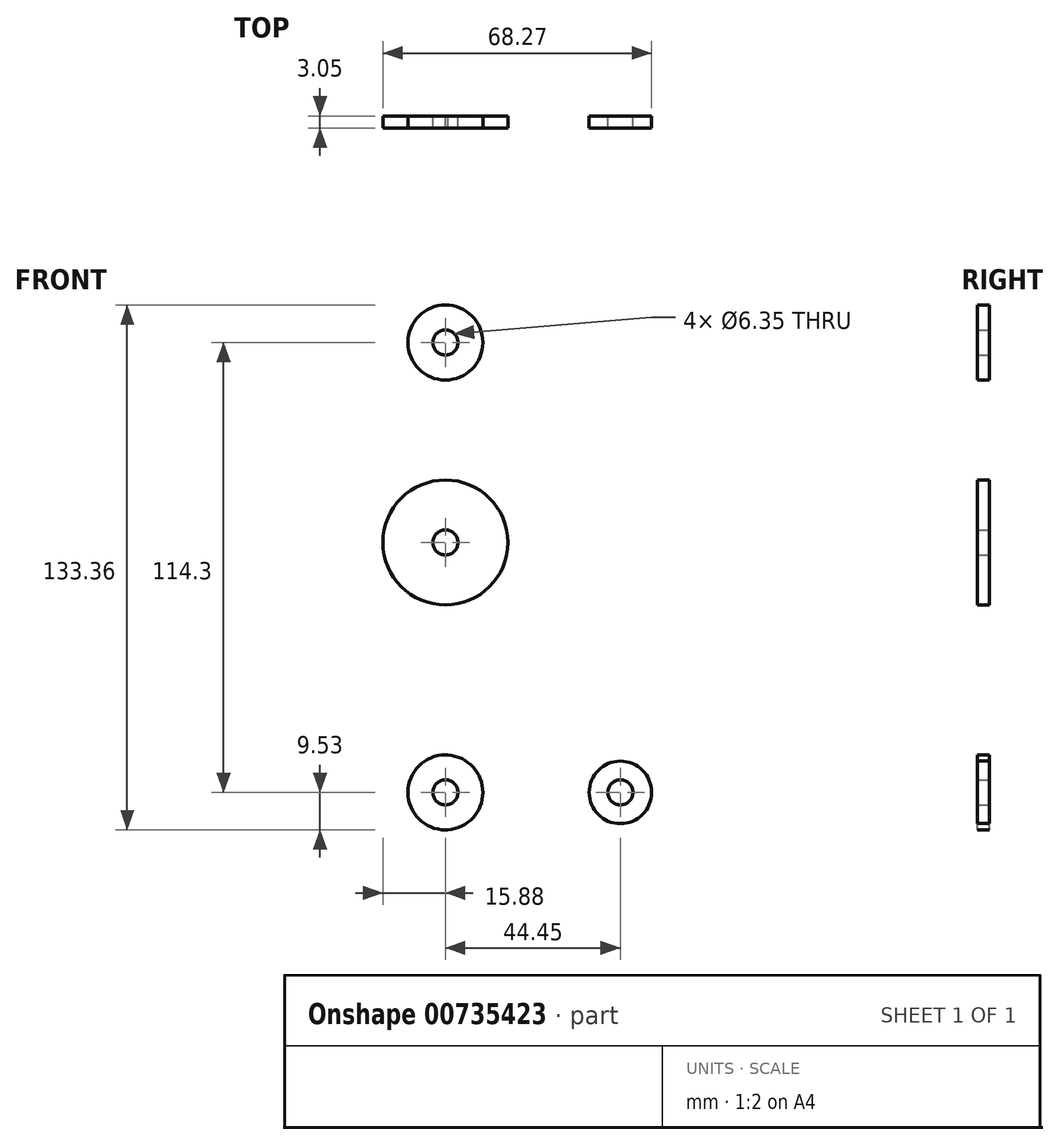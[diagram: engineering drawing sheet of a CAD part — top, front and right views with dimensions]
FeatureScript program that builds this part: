
annotation { "Feature Type Name" : "Feature", "Feature Type Description" : "" }
export const myFeature = defineFeature(function(context is Context, id is Id, definition is map)
    precondition{}
    {
        {
            var Q0;
            Q0=qCreatedBy(makeId("Front.planeOp"),FACE);
            var sketch = newSketch(context, id + "F0", { "sketchPlane" : qUnion([Q0])});
            skLineSegment(sketch, "E0", {"start": v(0, 0) * mm, "end": v(44.45, 0) * mm, "construction": true});
            skLineSegment(sketch, "E1", {"start": v(0, 0) * mm, "end": v(0, 114.3) * mm, "construction": true});
            skCircle(sketch, "E2", {"center": v(0, 114.3) * mm, "radius": 9.53 * mm});
            skCircle(sketch, "E3", {"center": v(0, 0) * mm, "radius": 9.53 * mm});
            skCircle(sketch, "E4", {"center": v(44.45, 0) * mm, "radius": 7.94 * mm});
            skCircle(sketch, "E5", {"center": v(0, 63.5) * mm, "radius": 15.88 * mm});
            skLineSegment(sketch, "E6", {"start": v(0, 9.53) * mm, "end": v(0.68, 9.5) * mm});
            skLineSegment(sketch, "E7", {"start": v(44.73, 7.93) * mm, "end": v(18.96, 8.85) * mm});
            skLineSegment(sketch, "E8", {"start": v(0, -9.53) * mm, "end": v(44.73, -7.93) * mm});
            skLineSegment(sketch, "E9", {"start": v(44.73, -7.93) * mm, "end": v(0, -9.53) * mm});
            skLineSegment(sketch, "E10", {"start": v(-9.45, 115.5) * mm, "end": v(-15.75, 65.48) * mm});
            skLineSegment(sketch, "E11", {"start": v(-15.75, 65.48) * mm, "end": v(-9.45, 115.5) * mm});
            skLineSegment(sketch, "E12", {"start": v(9.45, 115.5) * mm, "end": v(15.75, 65.48) * mm});
            skLineSegment(sketch, "E13", {"start": v(15.75, 65.48) * mm, "end": v(9.45, 115.5) * mm});
            skLineSegment(sketch, "E14", {"start": v(15.75, 61.91) * mm, "end": v(11.33, 17.58) * mm});
            skLineSegment(sketch, "E15", {"start": v(11.33, 17.58) * mm, "end": v(15.75, 61.91) * mm});
            skLineSegment(sketch, "E16", {"start": v(-15.8, 61.91) * mm, "end": v(-9.48, -0.95) * mm});
            skLineSegment(sketch, "E17", {"start": v(-9.48, -0.95) * mm, "end": v(-15.8, 61.91) * mm});
            skCircle(sketch, "E18", {"center": v(0, 114.3) * mm, "radius": 3.18 * mm});
            skCircle(sketch, "E19", {"center": v(-3.11, 99.9) * mm, "radius": 3.18 * mm});
            skCircle(sketch, "E20", {"center": v(0, 63.5) * mm, "radius": 3.18 * mm});
            skCircle(sketch, "E21", {"center": v(0, 0) * mm, "radius": 3.18 * mm});
            skCircle(sketch, "E22", {"center": v(44.45, 0) * mm, "radius": 3.18 * mm});
            skArc(sketch, "E23.filletArc", {"start": v(11.33, 17.58) * mm, "mid": v(13.25, 11.57) * mm, "end": v(18.96, 8.85) * mm});
            skLineSegment(sketch, "E24.trimOffspring", {"start": v(18.96, 8.85) * mm, "end": v(44.73, 7.93) * mm});
            skLineSegment(sketch, "E25.trimOffspring", {"start": v(9.57, 0) * mm, "end": v(9.48, -0.95) * mm});
            skSolve(sketch);
        }
        {
            var Q0;
            {var subQ1=sQuery(id+"F0.wireOp",EDGE,"E11");Q0=makeQuery(id+"F0.imprint","IMPRINT",FACE,{"disambiguationData":[TD([[makeQuery(id+"F0.imprint","IMPRINT",EDGE,{"derivedFrom":subQ1}),-1.0]])]});}
            var Q1;
            Q1=makeQuery(id+"F0.imprint","IMPRINT",FACE,{"disambiguationData":[TD([[makeQuery(id+"F0.imprint","IMPRINT",EDGE,{"derivedFrom":sQuery(id+"F0.wireOp",EDGE,"E18")}),-1.0]])]});
            var Q2;
            Q2=makeQuery(id+"F0.imprint","IMPRINT",FACE,{"disambiguationData":[TD([[makeQuery(id+"F0.imprint","IMPRINT",EDGE,{"derivedFrom":sQuery(id+"F0.wireOp",EDGE,"E20")}),-1.0]])]});
            var Q3;
            {var subQ0=sQuery(id+"F0.wireOp",EDGE,"E17");Q3=makeQuery(id+"F0.imprint","IMPRINT",FACE,{"disambiguationData":[TD([[makeQuery(id+"F0.imprint","IMPRINT",EDGE,{"derivedFrom":subQ0}),-1.0]])]});}
            var Q4;
            {var subQ0=sQuery(id+"F0.wireOp",EDGE,"E6");Q4=makeQuery(id+"F0.imprint","IMPRINT",FACE,{"disambiguationData":[TD([[makeQuery(id+"F0.imprint","IMPRINT",EDGE,{"derivedFrom":subQ0}),-1.0]])]});}
            var Q5;
            Q5=makeQuery(id+"F0.imprint","IMPRINT",FACE,{"disambiguationData":[TD([[makeQuery(id+"F0.imprint","IMPRINT",EDGE,{"derivedFrom":sQuery(id+"F0.wireOp",EDGE,"E22")}),-1.0]])]});
            extrude(context, id + "F1", {"entities" : qUnion([Q0, Q1, Q2, Q3, Q4, Q5]), "depth" : 3.05 * mm, "offsetDistance" : 25.4 * mm});
        }
    });
